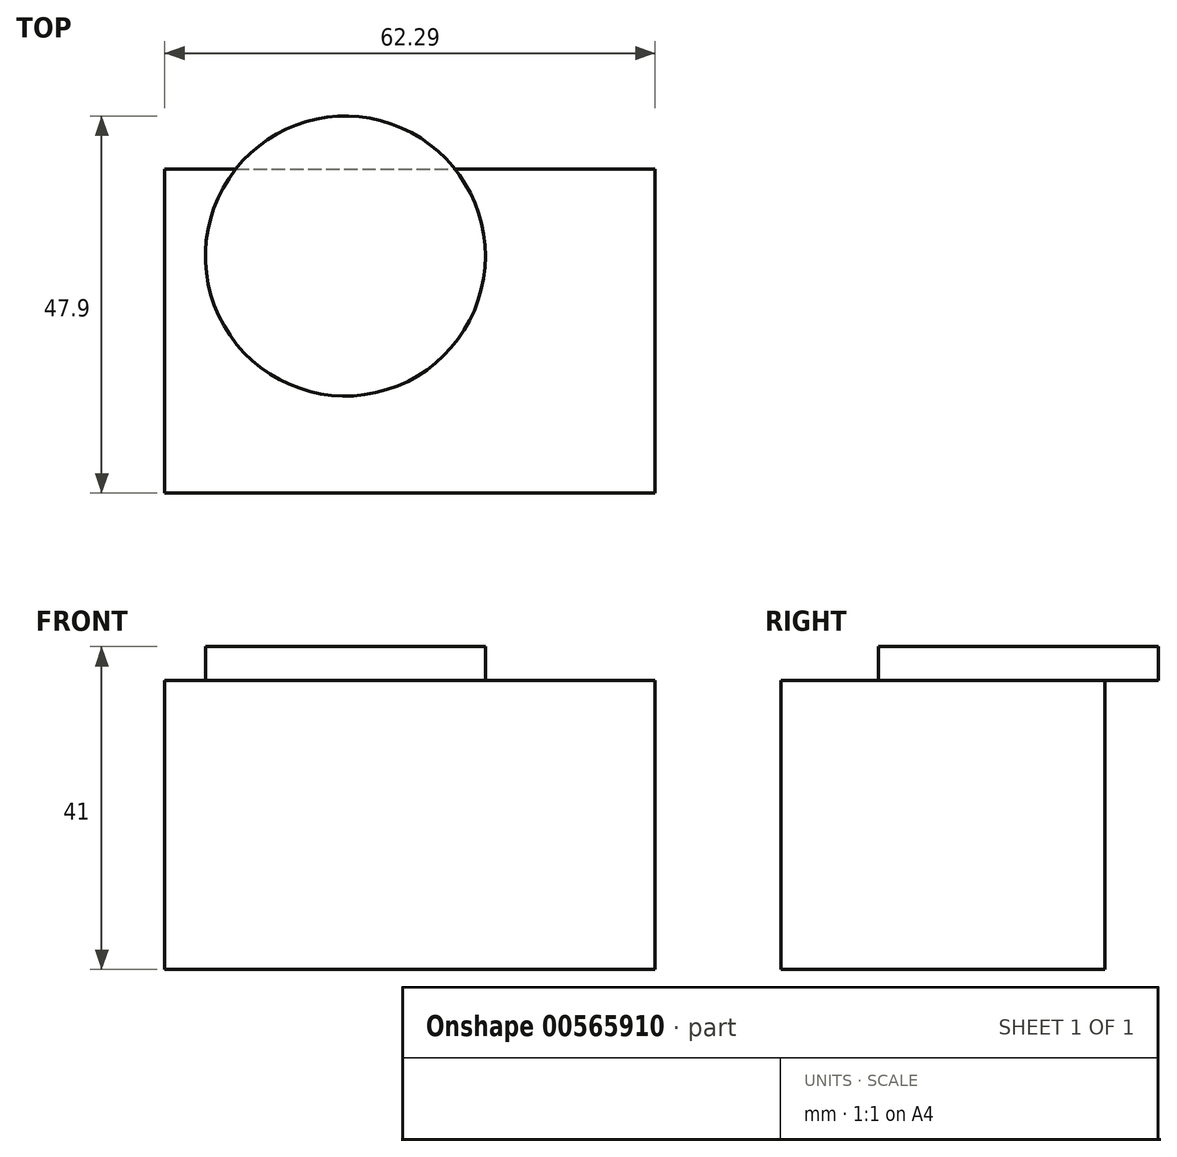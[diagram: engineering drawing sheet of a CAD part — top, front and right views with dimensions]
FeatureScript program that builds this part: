
annotation { "Feature Type Name" : "Feature", "Feature Type Description" : "" }
export const myFeature = defineFeature(function(context is Context, id is Id, definition is map)
    precondition{}
    {
        {
            var Q0;
            Q0=qCreatedBy(makeId("Front.planeOp"),FACE);
            var sketch = newSketch(context, id + "F0", { "sketchPlane" : qUnion([Q0])});
            skLineSegment(sketch, "E0.bottom", {"start": v(-62.29, 42.86) * mm, "end": v(0, 42.86) * mm});
            skLineSegment(sketch, "E0.top", {"start": v(-62.29, 6.17) * mm, "end": v(0, 6.17) * mm});
            skLineSegment(sketch, "E0.left", {"start": v(-62.29, 42.86) * mm, "end": v(-62.29, 6.17) * mm});
            skLineSegment(sketch, "E0.right", {"start": v(0, 42.86) * mm, "end": v(0, 6.17) * mm});
            skSolve(sketch);
        }
        {
            var Q0;
            Q0=makeQuery(id+"F0.imprint","IMPRINT",FACE,{"disambiguationData":[TD([[makeQuery(id+"F0.imprint","IMPRINT",EDGE,{"derivedFrom":sQuery(id+"F0.wireOp",EDGE,"E0.bottom")}),-1.0]])]});
            extrude(context, id + "F1", {"entities" : qUnion([Q0]), "depth" : 41.15 * mm, "offsetDistance" : 25.4 * mm});
        }
        {
            var Q0;
            Q0=makeQuery(id+"F1.opExtrude","SWEPT_FACE",FACE,{"disambiguationData":[OSD([sQuery(id+"F0.wireOp",EDGE,"E0.bottom")])]});
            var sketch = newSketch(context, id + "F2", { "sketchPlane" : qUnion([Q0])});
            skCircle(sketch, "E1", {"center": v(-39.35, -11.03) * mm, "radius": 17.78 * mm});
            skSolve(sketch);
        }
        {
            var Q0;
            Q0 = qSketchRegion(id + "F2", true);
            extrude(context, id + "F3", {"entities" : qUnion([Q0]), "operationType" : NewBodyOperationType.ADD, "depth" : 4.32 * mm, "offsetDistance" : 25.4 * mm});
        }
    });
